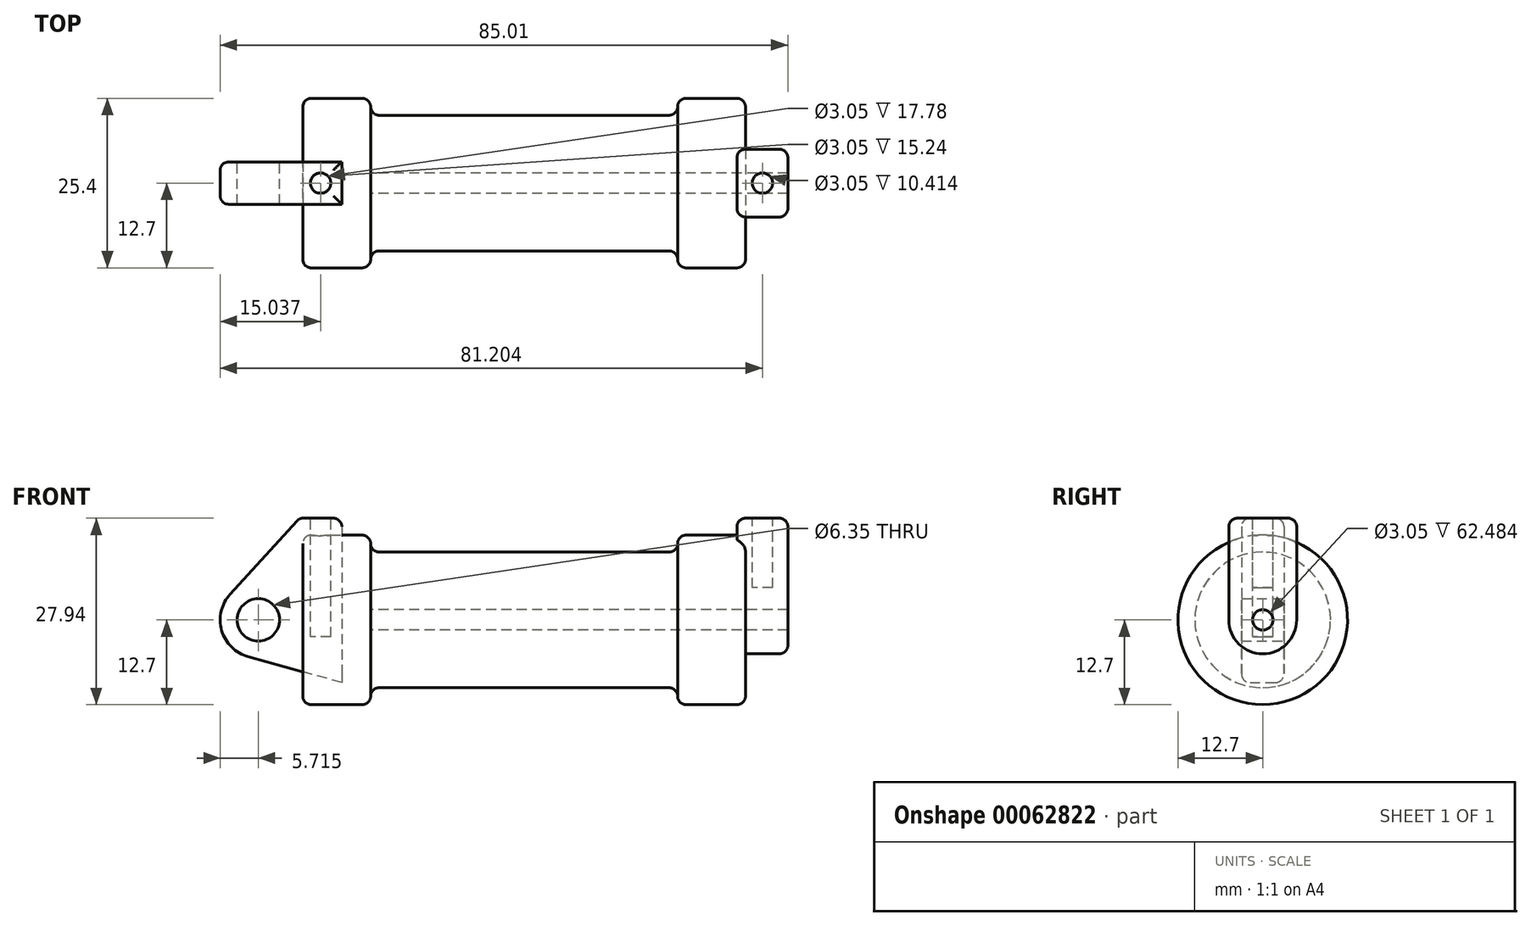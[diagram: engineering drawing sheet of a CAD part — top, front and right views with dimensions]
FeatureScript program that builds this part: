
annotation { "Feature Type Name" : "Feature", "Feature Type Description" : "" }
export const myFeature = defineFeature(function(context is Context, id is Id, definition is map)
    precondition{}
    {
        {
            var Q0;
            Q0=qCreatedBy(makeId("Front.planeOp"),FACE);
            var sketch = newSketch(context, id + "F0", { "sketchPlane" : qUnion([Q0])});
            skLineSegment(sketch, "E0", {"start": v(0, 0) * mm, "end": v(0, 12.7) * mm});
            skLineSegment(sketch, "E1", {"start": v(0, 12.7) * mm, "end": v(10.16, 12.7) * mm});
            skLineSegment(sketch, "E2", {"start": v(10.16, 12.7) * mm, "end": v(10.16, 10.16) * mm});
            skLineSegment(sketch, "E3", {"start": v(10.16, 10.16) * mm, "end": v(56.13, 10.16) * mm});
            skLineSegment(sketch, "E4", {"start": v(56.13, 10.16) * mm, "end": v(56.13, 12.7) * mm});
            skLineSegment(sketch, "E5", {"start": v(56.13, 12.7) * mm, "end": v(66.3, 12.7) * mm});
            skLineSegment(sketch, "E6", {"start": v(66.3, 12.7) * mm, "end": v(66.3, 0) * mm});
            skLineSegment(sketch, "E7", {"start": v(66.3, 0) * mm, "end": v(0, 0) * mm});
            skLineSegment(sketch, "E8", {"start": v(5.84, 15.24) * mm, "end": v(-0.5, 15.24) * mm});
            skLineSegment(sketch, "E9", {"start": v(-0.5, 15.24) * mm, "end": v(-10.88, 3.85) * mm});
            skLineSegment(sketch, "E10", {"start": v(0, 0) * mm, "end": v(-6.65, 0) * mm});
            skCircle(sketch, "E11", {"center": v(-6.65, 0) * mm, "radius": 5.72 * mm});
            skCircle(sketch, "E12", {"center": v(-6.65, 0) * mm, "radius": 3.18 * mm});
            skLineSegment(sketch, "E13", {"start": v(5.84, 15.24) * mm, "end": v(5.84, -9.4) * mm});
            skLineSegment(sketch, "E14", {"start": v(5.84, -9.4) * mm, "end": v(-8.18, -5.5) * mm});
            skSolve(sketch);
        }
        {
            var Q0;
            {var subQ0=sQuery(id+"F0.wireOp",EDGE,"E2");Q0=makeQuery(id+"F0.imprint","IMPRINT",FACE,{"disambiguationData":[TD([[makeQuery(id+"F0.imprint","IMPRINT",EDGE,{"derivedFrom":subQ0}),-1.0]])]});}
            var Q1;
            {var subQ0=sQuery(id+"F0.wireOp",EDGE,"E0");Q1=makeQuery(id+"F0.imprint","IMPRINT",FACE,{"disambiguationData":[TD([[makeQuery(id+"F0.imprint","IMPRINT",EDGE,{"derivedFrom":subQ0}),-1.0]])]});}
            var Q2;
            Q2=sQuery(id+"F0.wireOp",EDGE,"E7");
            revolve(context, id + "F1", {"entities" : qUnion([Q0, Q1]), "axis" : qUnion([Q2]), "revolveType" : RevolveType.FULL});
        }
        {
            var Q0;
            {var subQ3=sQuery(id+"F0.wireOp",EDGE,"E0");Q0=makeQuery(id+"F0.imprint","IMPRINT",FACE,{"disambiguationData":[TD([[makeQuery(id+"F0.imprint","IMPRINT",EDGE,{"derivedFrom":subQ3}),1.0]])]});}
            var Q1;
            {var subQ4=sQuery(id+"F0.wireOp",EDGE,"E12");Q1=makeQuery(id+"F0.imprint","IMPRINT",FACE,{"disambiguationData":[TD([[makeQuery(id+"F0.imprint","IMPRINT",EDGE,{"derivedFrom":subQ4}),-1.0]])]});}
            var Q2;
            {var subQ0=sQuery(id+"F0.wireOp",EDGE,"E14");Q2=makeQuery(id+"F0.imprint","IMPRINT",FACE,{"disambiguationData":[TD([[makeQuery(id+"F0.imprint","IMPRINT",EDGE,{"derivedFrom":subQ0}),-1.0]])]});}
            var Q3;
            {var subQ0=sQuery(id+"F0.wireOp",EDGE,"E0");Q3=makeQuery(id+"F0.imprint","IMPRINT",FACE,{"disambiguationData":[TD([[makeQuery(id+"F0.imprint","IMPRINT",EDGE,{"derivedFrom":subQ0}),-1.0]])]});}
            extrude(context, id + "F2", {"entities" : qUnion([Q0, Q1, Q2, Q3]), "endBound" : BoundingType.SYMMETRIC, "depth" : 6.35 * mm});
        }
        {
            var Q0;
            Q0=makeQuery(id+"F1.opRevolve","SWEPT_FACE",FACE,{"disambiguationData":[OSD([sQuery(id+"F0.wireOp",EDGE,"E6")])]});
            var sketch = newSketch(context, id + "F3", { "sketchPlane" : qUnion([Q0])});
            skCircle(sketch, "E15", {"center": v(0, 0) * mm, "radius": 1.52 * mm});
            skCircle(sketch, "E16", {"center": v(0, 0) * mm, "radius": 5.08 * mm});
            skLineSegment(sketch, "E17", {"start": v(-5.08, 0) * mm, "end": v(-5.08, 15.24) * mm});
            skLineSegment(sketch, "E18", {"start": v(5.08, 0) * mm, "end": v(5.08, 15.24) * mm});
            skLineSegment(sketch, "E19", {"start": v(-5.08, 15.24) * mm, "end": v(5.08, 15.24) * mm});
            skSolve(sketch);
        }
        {
            var Q0;
            {var subQ0=sQuery(id+"F3.wireOp",EDGE,"E19");Q0=makeQuery(id+"F3.imprint","IMPRINT",FACE,{"disambiguationData":[TD([[makeQuery(id+"F3.imprint","IMPRINT",EDGE,{"derivedFrom":subQ0}),-1.0]])]});}
            var Q1;
            {var subQ0=sQuery(id+"F3.wireOp",EDGE,"E17");var subQ1=sQuery(id+"F3.wireOp",EDGE,"E16");var subQ2=makeQuery(id+"F3.imprint","INTERSECT",VERTEX,{"derivedFrom":[subQ1,subQ0]});Q1=makeQuery(id+"F3.imprint","IMPRINT",FACE,{"disambiguationData":[TD([[makeQuery(id+"F3.imprint","IMPRINT",EDGE,{"disambiguationData":[TD([[subQ2,1.0]])],"derivedFrom":subQ1}),-1.0]])]});}
            var Q2;
            Q2=makeQuery(id+"F3.imprint","IMPRINT",FACE,{"disambiguationData":[TD([[makeQuery(id+"F3.imprint","IMPRINT",EDGE,{"derivedFrom":sQuery(id+"F3.wireOp",EDGE,"E15")}),-1.0]])]});
            extrude(context, id + "F4", {"entities" : qUnion([Q0, Q1, Q2]), "operationType" : NewBodyOperationType.ADD, "depth" : 6.35 * mm});
        }
        {
            var Q0;
            Q0=makeQuery(id+"F4.opExtrude","CAP_FACE",FACE,{"disambiguationData":[OSD([sQuery(id+"F3.wireOp",EDGE,"E15"),sQuery(id+"F3.wireOp",EDGE,"E16"),sQuery(id+"F3.wireOp",EDGE,"E17"),sQuery(id+"F3.wireOp",EDGE,"E18"),sQuery(id+"F3.wireOp",EDGE,"E19")])],"isStart":false});
            extrude(context, id + "F5", {"entities" : qUnion([Q0]), "operationType" : NewBodyOperationType.ADD, "oppositeDirection" : true, "depth" : 7.62 * mm});
        }
        {
            var Q0;
            Q0=makeQuery(id+"F4.boolean.opBoolean","SPLIT",FACE,{"disambiguationData":[TD([makeQuery(id+"F4.opExtrude","SWEPT_FACE",FACE,{"disambiguationData":[OSD([sQuery(id+"F3.wireOp",EDGE,"E15")])]})])],"derivedFrom":makeQuery(id+"F1.opRevolve","SWEPT_FACE",FACE,{"disambiguationData":[OSD([sQuery(id+"F0.wireOp",EDGE,"E6")])]})});
            var Q1;
            Q1=makeQuery(id+"F1.opRevolve","SWEPT_FACE",FACE,{"disambiguationData":[OSD([sQuery(id+"F0.wireOp",EDGE,"E2")])]});
            extrude(context, id + "F6", {"entities" : qUnion([Q0]), "operationType" : NewBodyOperationType.REMOVE, "endBound" : BoundingType.UP_TO_SURFACE, "oppositeDirection" : true, "endBoundEntityFace" : qUnion([Q1]), "depth" : 25.4 * mm});
        }
        {
            var Q0;
            Q0=makeQuery(id+"F2.opExtrude","SWEPT_FACE",FACE,{"disambiguationData":[OSD([sQuery(id+"F0.wireOp",EDGE,"E8")])]});
            var sketch = newSketch(context, id + "F7", { "sketchPlane" : qUnion([Q0])});
            skCircle(sketch, "E20", {"center": v(2.67, 0) * mm, "radius": 1.52 * mm});
            skPoint(sketch, "E20.centerSnap0", {"position": v(2.67, 3.18) * mm});
            skPoint(sketch, "E20.centerSnap1", {"position": v(-0.5, 0) * mm});
            skSolve(sketch);
        }
        {
            var Q0;
            {var subQ0=sQuery(id+"F3.wireOp",EDGE,"E19");Q0=makeQuery(id+"F5.boolean.opBoolean","MERGE",FACE,{"derivedFrom":[makeQuery(id+"F4.opExtrude","SWEPT_FACE",FACE,{"disambiguationData":[OSD([subQ0])]}),makeQuery(id+"F5.opExtrude","SWEPT_FACE",FACE,{"disambiguationData":[OSD([subQ0])]})]});}
            var sketch = newSketch(context, id + "F8", { "sketchPlane" : qUnion([Q0])});
            skCircle(sketch, "E21", {"center": v(68.83, 0) * mm, "radius": 1.52 * mm});
            skPoint(sketch, "E21.centerSnap0", {"position": v(68.83, 5.08) * mm});
            skPoint(sketch, "E21.centerSnap1", {"position": v(65.02, 0) * mm});
            skSolve(sketch);
        }
        {
            var Q0;
            Q0=makeQuery(id+"F7.imprint","IMPRINT",FACE,{"disambiguationData":[TD([[makeQuery(id+"F7.imprint","IMPRINT",EDGE,{"derivedFrom":sQuery(id+"F7.wireOp",EDGE,"E20")}),1.0]])]});
            extrude(context, id + "F9", {"entities" : qUnion([Q0]), "operationType" : NewBodyOperationType.REMOVE, "oppositeDirection" : true, "depth" : 17.78 * mm});
        }
        {
            var Q0;
            Q0=makeQuery(id+"F8.imprint","IMPRINT",FACE,{"disambiguationData":[TD([[makeQuery(id+"F8.imprint","IMPRINT",EDGE,{"derivedFrom":sQuery(id+"F8.wireOp",EDGE,"E21")}),1.0]])]});
            extrude(context, id + "F10", {"entities" : qUnion([Q0]), "operationType" : NewBodyOperationType.REMOVE, "oppositeDirection" : true, "depth" : 10.4 * mm});
        }
        {
            var Q0;
            Q0=makeQuery(id+"F1.opRevolve","SWEPT_EDGE",EDGE,{"disambiguationData":[OSD([sQuery(id+"F0.wireOp",EDGE,"E0"),sQuery(id+"F0.wireOp",EDGE,"E1")])]});
            var Q1;
            Q1=makeQuery(id+"F1.opRevolve","SWEPT_EDGE",EDGE,{"disambiguationData":[OSD([sQuery(id+"F0.wireOp",EDGE,"E1"),sQuery(id+"F0.wireOp",EDGE,"E2")])]});
            var Q2;
            Q2=makeQuery(id+"F1.opRevolve","SWEPT_EDGE",EDGE,{"disambiguationData":[OSD([sQuery(id+"F0.wireOp",EDGE,"E4"),sQuery(id+"F0.wireOp",EDGE,"E5")])]});
            var Q3;
            Q3=makeQuery(id+"F4.boolean.opBoolean","SPLIT",EDGE,{"disambiguationData":[OD(1.0)],"derivedFrom":makeQuery(id+"F1.opRevolve","SWEPT_EDGE",EDGE,{"disambiguationData":[OSD([sQuery(id+"F0.wireOp",EDGE,"E5"),sQuery(id+"F0.wireOp",EDGE,"E6")])]})});
            var Q4;
            Q4=makeQuery(id+"F1.opRevolve","SWEPT_EDGE",EDGE,{"disambiguationData":[OSD([sQuery(id+"F0.wireOp",EDGE,"E2"),sQuery(id+"F0.wireOp",EDGE,"E3")])]});
            var Q5;
            Q5=makeQuery(id+"F1.opRevolve","SWEPT_EDGE",EDGE,{"disambiguationData":[OSD([sQuery(id+"F0.wireOp",EDGE,"E3"),sQuery(id+"F0.wireOp",EDGE,"E4")])]});
            fillet(context, id + "F11", {"entities" : qUnion([Q0, Q1, Q2, Q3, Q4, Q5]), "radius" : 1.27 * mm, "tangentPropagation" : true, "allowEdgeOverflow" : false});
        }
        {
            var Q0;
            Q0=makeQuery(id+"F2.opExtrude","SWEPT_FACE",FACE,{"disambiguationData":[OSD([sQuery(id+"F0.wireOp",EDGE,"E9")])]});
            var Q1;
            Q1=makeQuery(id+"F2.opExtrude","CAP_EDGE",EDGE,{"disambiguationData":[OSD([sQuery(id+"F0.wireOp",EDGE,"E8")])],"isStart":true});
            var Q2;
            Q2=makeQuery(id+"F2.opExtrude","CAP_EDGE",EDGE,{"disambiguationData":[OSD([sQuery(id+"F0.wireOp",EDGE,"E8")])],"isStart":false});
            var Q3;
            Q3=makeQuery(id+"F2.opExtrude","SWEPT_EDGE",EDGE,{"disambiguationData":[OSD([sQuery(id+"F0.wireOp",EDGE,"E8"),sQuery(id+"F0.wireOp",EDGE,"E13")])]});
            fillet(context, id + "F12", {"entities" : qUnion([Q0, Q1, Q2, Q3]), "radius" : 1.27 * mm, "tangentPropagation" : true, "allowEdgeOverflow" : false});
        }
        {
            var Q0;
            Q0=makeQuery(id+"F4.opExtrude","CAP_EDGE",EDGE,{"disambiguationData":[OSD([sQuery(id+"F3.wireOp",EDGE,"E19")])],"isStart":false});
            var Q1;
            {var subQ0=sQuery(id+"F3.wireOp",EDGE,"E19");var subQ1=sQuery(id+"F3.wireOp",EDGE,"E17");Q1=makeQuery(id+"F5.boolean.opBoolean","MERGE",EDGE,{"derivedFrom":[makeQuery(id+"F4.opExtrude","SWEPT_EDGE",EDGE,{"disambiguationData":[OSD([subQ1,subQ0])]}),makeQuery(id+"F5.opExtrude","SWEPT_EDGE",EDGE,{"disambiguationData":[OSD([subQ1,subQ0])]})]});}
            var Q2;
            Q2=makeQuery(id+"F5.opExtrude","CAP_EDGE",EDGE,{"disambiguationData":[OSD([sQuery(id+"F3.wireOp",EDGE,"E17")])],"isStart":false});
            var Q3;
            Q3=makeQuery(id+"F5.opExtrude","CAP_EDGE",EDGE,{"disambiguationData":[OSD([sQuery(id+"F3.wireOp",EDGE,"E19")])],"isStart":false});
            var Q4;
            {var subQ0=sQuery(id+"F3.wireOp",EDGE,"E19");var subQ1=sQuery(id+"F3.wireOp",EDGE,"E18");Q4=makeQuery(id+"F5.boolean.opBoolean","MERGE",EDGE,{"derivedFrom":[makeQuery(id+"F4.opExtrude","SWEPT_EDGE",EDGE,{"disambiguationData":[OSD([subQ1,subQ0])]}),makeQuery(id+"F5.opExtrude","SWEPT_EDGE",EDGE,{"disambiguationData":[OSD([subQ1,subQ0])]})]});}
            var Q5;
            Q5=makeQuery(id+"F4.opExtrude","CAP_EDGE",EDGE,{"disambiguationData":[OSD([sQuery(id+"F3.wireOp",EDGE,"E17")])],"isStart":false});
            var Q6;
            Q6=makeQuery(id+"F5.opExtrude","CAP_EDGE",EDGE,{"disambiguationData":[OSD([sQuery(id+"F3.wireOp",EDGE,"E18")])],"isStart":false});
            fillet(context, id + "F13", {"entities" : qUnion([Q0, Q1, Q2, Q3, Q4, Q5, Q6]), "radius" : 1.27 * mm, "tangentPropagation" : true, "allowEdgeOverflow" : false});
        }
    });
